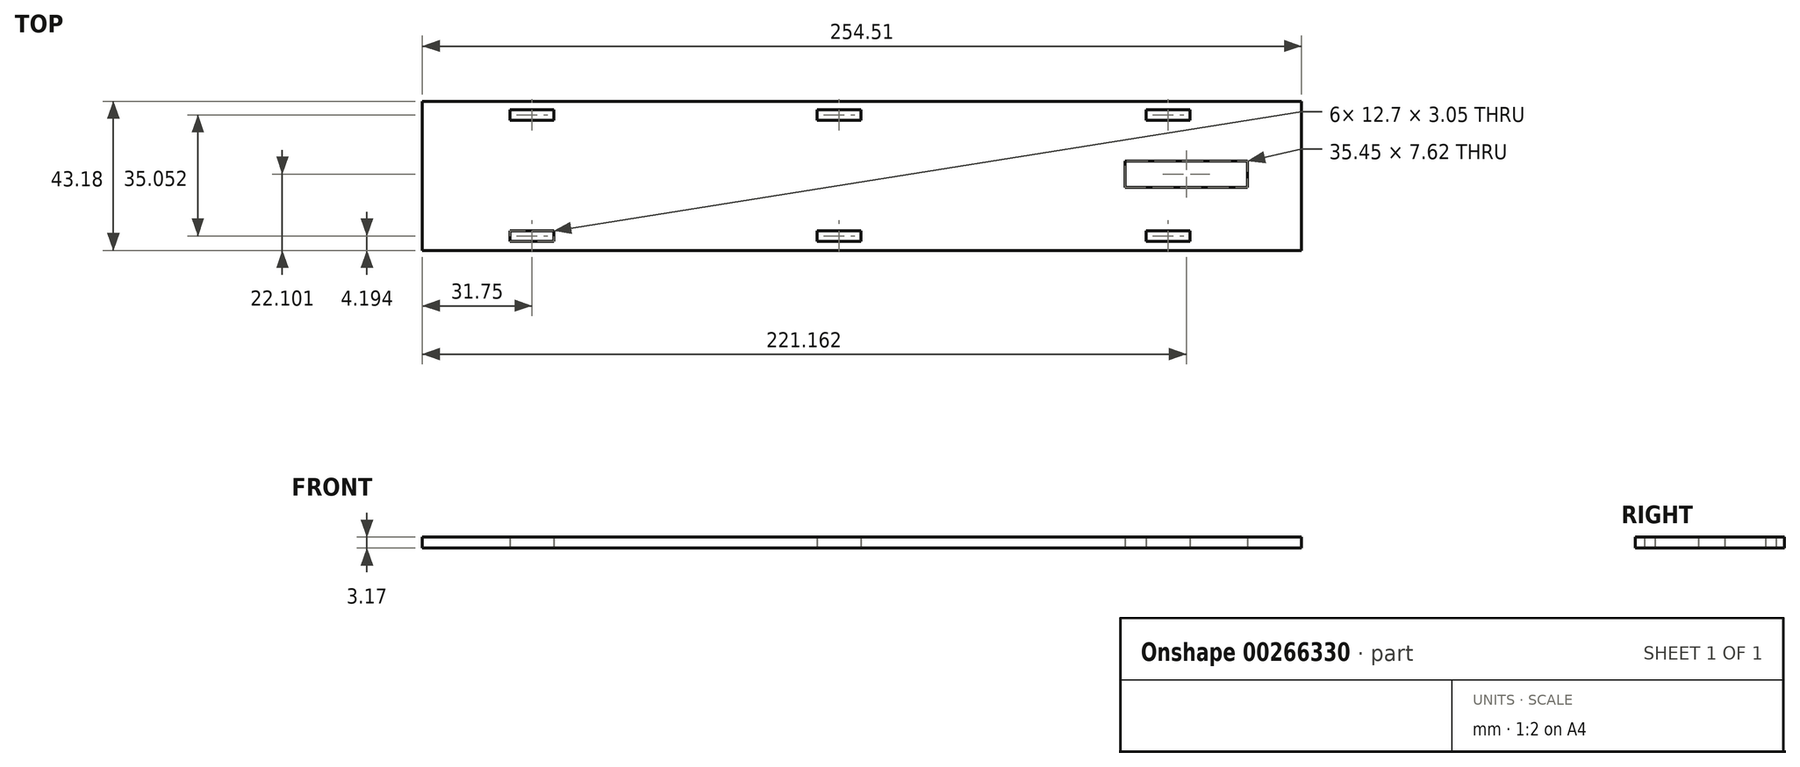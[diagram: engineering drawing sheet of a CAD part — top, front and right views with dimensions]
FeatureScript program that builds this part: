
annotation { "Feature Type Name" : "Feature", "Feature Type Description" : "" }
export const myFeature = defineFeature(function(context is Context, id is Id, definition is map)
    precondition{}
    {
        {
            var Q0;
            Q0=qCreatedBy(makeId("Top.planeOp"),FACE);
            var sketch = newSketch(context, id + "F0", { "sketchPlane" : qUnion([Q0])});
            skLineSegment(sketch, "E0.left", {"start": v(-127, -21.4) * mm, "end": v(-127, 21.77) * mm});
            skLineSegment(sketch, "E1.bottom", {"start": v(-101.6, -15.7) * mm, "end": v(-88.9, -15.7) * mm});
            skLineSegment(sketch, "E1.top", {"start": v(-101.6, -18.74) * mm, "end": v(-88.9, -18.74) * mm});
            skLineSegment(sketch, "E1.left", {"start": v(-101.6, -15.7) * mm, "end": v(-101.6, -18.74) * mm});
            skLineSegment(sketch, "E1.right", {"start": v(-88.9, -15.7) * mm, "end": v(-88.9, -18.74) * mm});
            skLineSegment(sketch, "E2.bottom", {"start": v(-12.7, -18.74) * mm, "end": v(0, -18.74) * mm});
            skLineSegment(sketch, "E2.top", {"start": v(-12.7, -15.7) * mm, "end": v(0, -15.7) * mm});
            skLineSegment(sketch, "E2.left", {"start": v(-12.7, -18.74) * mm, "end": v(-12.7, -15.7) * mm});
            skLineSegment(sketch, "E2.right", {"start": v(0, -18.74) * mm, "end": v(0, -15.7) * mm});
            skLineSegment(sketch, "E3.bottom", {"start": v(82.55, -18.74) * mm, "end": v(95.25, -18.74) * mm});
            skLineSegment(sketch, "E3.top", {"start": v(82.55, -15.7) * mm, "end": v(95.25, -15.7) * mm});
            skLineSegment(sketch, "E3.left", {"start": v(82.55, -18.74) * mm, "end": v(82.55, -15.7) * mm});
            skLineSegment(sketch, "E3.right", {"start": v(95.25, -18.74) * mm, "end": v(95.25, -15.7) * mm});
            skLineSegment(sketch, "E4.bottom", {"start": v(-101.6, 19.36) * mm, "end": v(-88.9, 19.36) * mm});
            skLineSegment(sketch, "E4.top", {"start": v(-101.6, 16.31) * mm, "end": v(-88.9, 16.31) * mm});
            skLineSegment(sketch, "E4.left", {"start": v(-101.6, 19.36) * mm, "end": v(-101.6, 16.31) * mm});
            skLineSegment(sketch, "E4.right", {"start": v(-88.9, 19.36) * mm, "end": v(-88.9, 16.31) * mm});
            skLineSegment(sketch, "E5.bottom", {"start": v(-12.7, 19.36) * mm, "end": v(0, 19.36) * mm});
            skLineSegment(sketch, "E5.top", {"start": v(-12.7, 16.31) * mm, "end": v(0, 16.31) * mm});
            skLineSegment(sketch, "E5.left", {"start": v(-12.7, 19.36) * mm, "end": v(-12.7, 16.31) * mm});
            skLineSegment(sketch, "E5.right", {"start": v(0, 19.36) * mm, "end": v(0, 16.31) * mm});
            skLineSegment(sketch, "E6.bottom", {"start": v(82.55, 19.36) * mm, "end": v(95.25, 19.36) * mm});
            skLineSegment(sketch, "E6.top", {"start": v(82.55, 16.31) * mm, "end": v(95.25, 16.31) * mm});
            skLineSegment(sketch, "E6.left", {"start": v(82.55, 19.36) * mm, "end": v(82.55, 16.31) * mm});
            skLineSegment(sketch, "E6.right", {"start": v(95.25, 19.36) * mm, "end": v(95.25, 16.31) * mm});
            skLineSegment(sketch, "E7.bottom", {"start": v(76.44, -3.12) * mm, "end": v(78.96, -3.12) * mm});
            skLineSegment(sketch, "E7.top", {"start": v(76.44, 4.5) * mm, "end": v(78.96, 4.5) * mm});
            skLineSegment(sketch, "E7.left", {"start": v(76.44, -3.12) * mm, "end": v(76.44, 4.5) * mm});
            skLineSegment(sketch, "E8.bottom", {"start": v(78.96, -3.12) * mm, "end": v(111.89, -3.12) * mm});
            skLineSegment(sketch, "E8.top", {"start": v(78.96, 4.5) * mm, "end": v(111.89, 4.5) * mm});
            skLineSegment(sketch, "E9", {"start": v(111.89, 4.5) * mm, "end": v(111.89, -3.12) * mm});
            skPoint(sketch, "E8.right.end.orphan", {"position": v(114.54, 4.5) * mm});
            skPoint(sketch, "E10.orphan", {"position": v(114.54, -3.12) * mm});
            skLineSegment(sketch, "E11", {"start": v(127.5, 21.77) * mm, "end": v(-127, 21.77) * mm});
            skPoint(sketch, "E12.right.end.orphan", {"position": v(127.5, 23.04) * mm});
            skPoint(sketch, "E12.right.start.orphan", {"position": v(128.02, 23.55) * mm});
            skPoint(sketch, "E13.right.start.orphan", {"position": v(127.5, -21.4) * mm});
            skPoint(sketch, "E13.top.end.orphan", {"position": v(127, -20.9) * mm});
            skLineSegment(sketch, "E14", {"start": v(-127, -21.4) * mm, "end": v(127.5, -21.4) * mm});
            skLineSegment(sketch, "E15.trimOffspring", {"start": v(127.5, -21.4) * mm, "end": v(127.5, 21.77) * mm});
            skPoint(sketch, "E0.right.start.orphan", {"position": v(127, -21.53) * mm});
            skSolve(sketch);
        }
        {
            var Q0;
            Q0=makeQuery(id+"F0.imprint","IMPRINT",FACE,{"disambiguationData":[TD([[makeQuery(id+"F0.imprint","IMPRINT",EDGE,{"derivedFrom":sQuery(id+"F0.wireOp",EDGE,"E0.bottom")}),1.0]])]});
            var Q1;
            Q1=makeQuery(id+"F0.imprint","IMPRINT",FACE,{"disambiguationData":[TD([[makeQuery(id+"F0.imprint","IMPRINT",EDGE,{"derivedFrom":sQuery(id+"F0.wireOp",EDGE,"E0.left")}),-1.0]])]});
            extrude(context, id + "F1", {"entities" : qUnion([Q0, Q1]), "depth" : 3.17 * mm});
        }
    });
